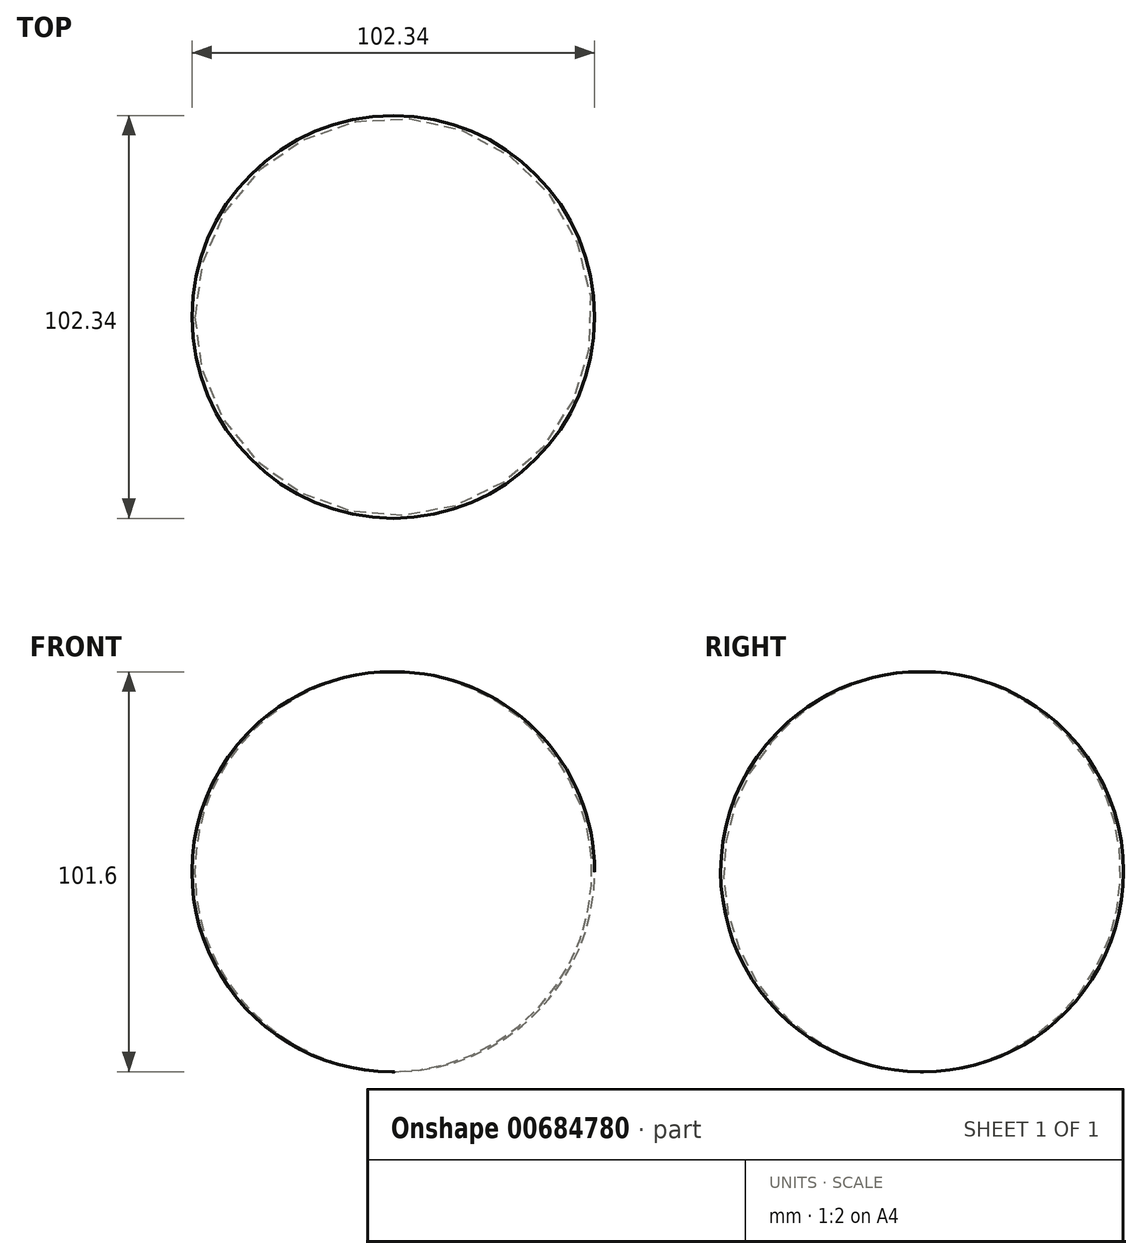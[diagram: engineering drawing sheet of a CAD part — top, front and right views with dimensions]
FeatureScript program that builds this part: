
annotation { "Feature Type Name" : "Feature", "Feature Type Description" : "" }
export const myFeature = defineFeature(function(context is Context, id is Id, definition is map)
    precondition{}
    {
        {
            var Q0;
            Q0=qCreatedBy(makeId("Front.planeOp"),FACE);
            var sketch = newSketch(context, id + "F0", { "sketchPlane" : qUnion([Q0])});
            skLineSegment(sketch, "E0", {"start": v(0, 0) * mm, "end": v(0, -101.6) * mm});
            skArc(sketch, "E1", {"start": v(0, 0) * mm, "mid": v(-50.44, -50.8) * mm, "end": v(0, -101.6) * mm});
            skSolve(sketch);
        }
        {
            var Q0;
            Q0=makeQuery(id+"F0.imprint","IMPRINT",FACE,{"disambiguationData":[TD([[makeQuery(id+"F0.imprint","IMPRINT",EDGE,{"derivedFrom":sQuery(id+"F0.wireOp",EDGE,"E0")}),-1.0]])]});
            var Q1;
            Q1=sQuery(id+"F0.wireOp",EDGE,"E0");
            revolve(context, id + "F1", {"entities" : qUnion([Q0]), "axis" : qUnion([Q1]), "revolveType" : RevolveType.FULL});
        }
    });
